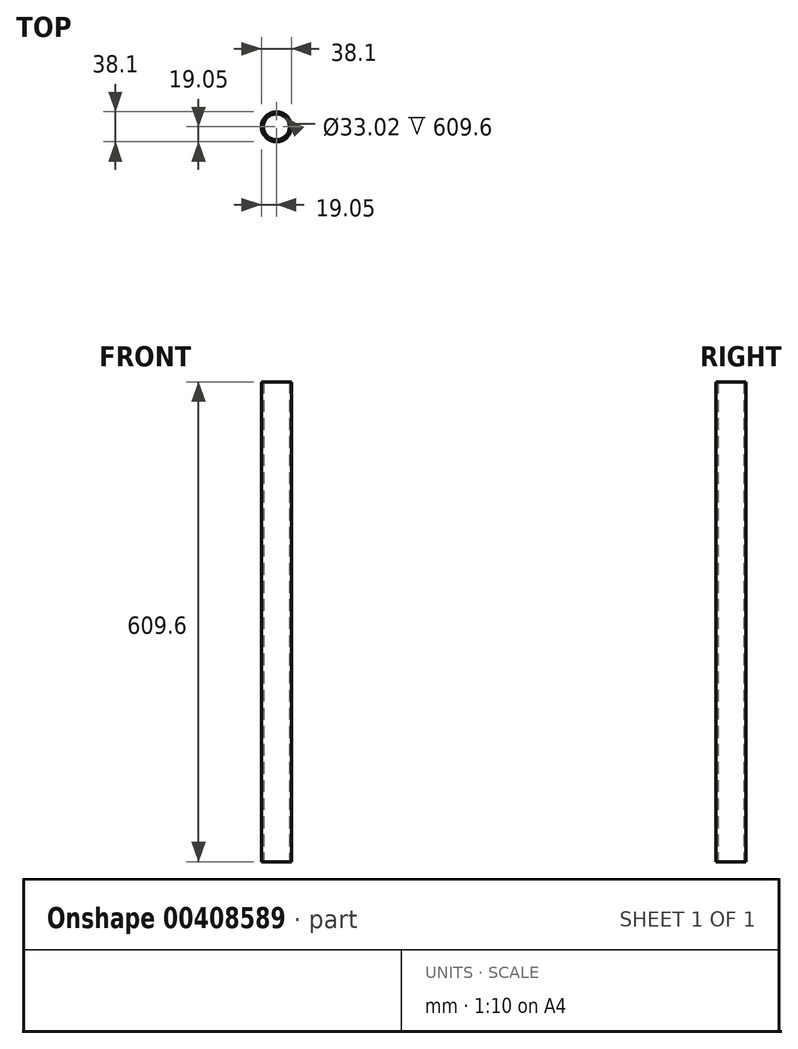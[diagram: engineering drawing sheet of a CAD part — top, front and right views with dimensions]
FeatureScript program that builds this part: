
annotation { "Feature Type Name" : "Feature", "Feature Type Description" : "" }
export const myFeature = defineFeature(function(context is Context, id is Id, definition is map)
    precondition{}
    {
        {
            var Q0;
            Q0=qCreatedBy(makeId("Top.planeOp"),FACE);
            var sketch = newSketch(context, id + "F0", { "sketchPlane" : qUnion([Q0])});
            skCircle(sketch, "E0", {"center": v(0, 0) * mm, "radius": 19.05 * mm});
            skSolve(sketch);
        }
        {
            var Q0;
            Q0=makeQuery(id+"F0.imprint","IMPRINT",FACE,{"disambiguationData":[TD([[makeQuery(id+"F0.imprint","IMPRINT",EDGE,{"derivedFrom":sQuery(id+"F0.wireOp",EDGE,"E0")}),1.0]])]});
            extrude(context, id + "F1", {"entities" : qUnion([Q0]), "endBound" : BoundingType.SYMMETRIC, "depth" : 609.6 * mm});
        }
        {
            var Q0;
            Q0=makeQuery(id+"F1.opExtrude","CAP_FACE",FACE,{"disambiguationData":[OSD([sQuery(id+"F0.wireOp",EDGE,"E0")])],"isStart":false});
            var Q1;
            Q1=makeQuery(id+"F1.opExtrude","CAP_FACE",FACE,{"disambiguationData":[OSD([sQuery(id+"F0.wireOp",EDGE,"E0")])],"isStart":true});
            shell(context, id + "F2", {"entities" : qUnion([Q0, Q1]), "thickness" : 2.54 * mm});
        }
    });
